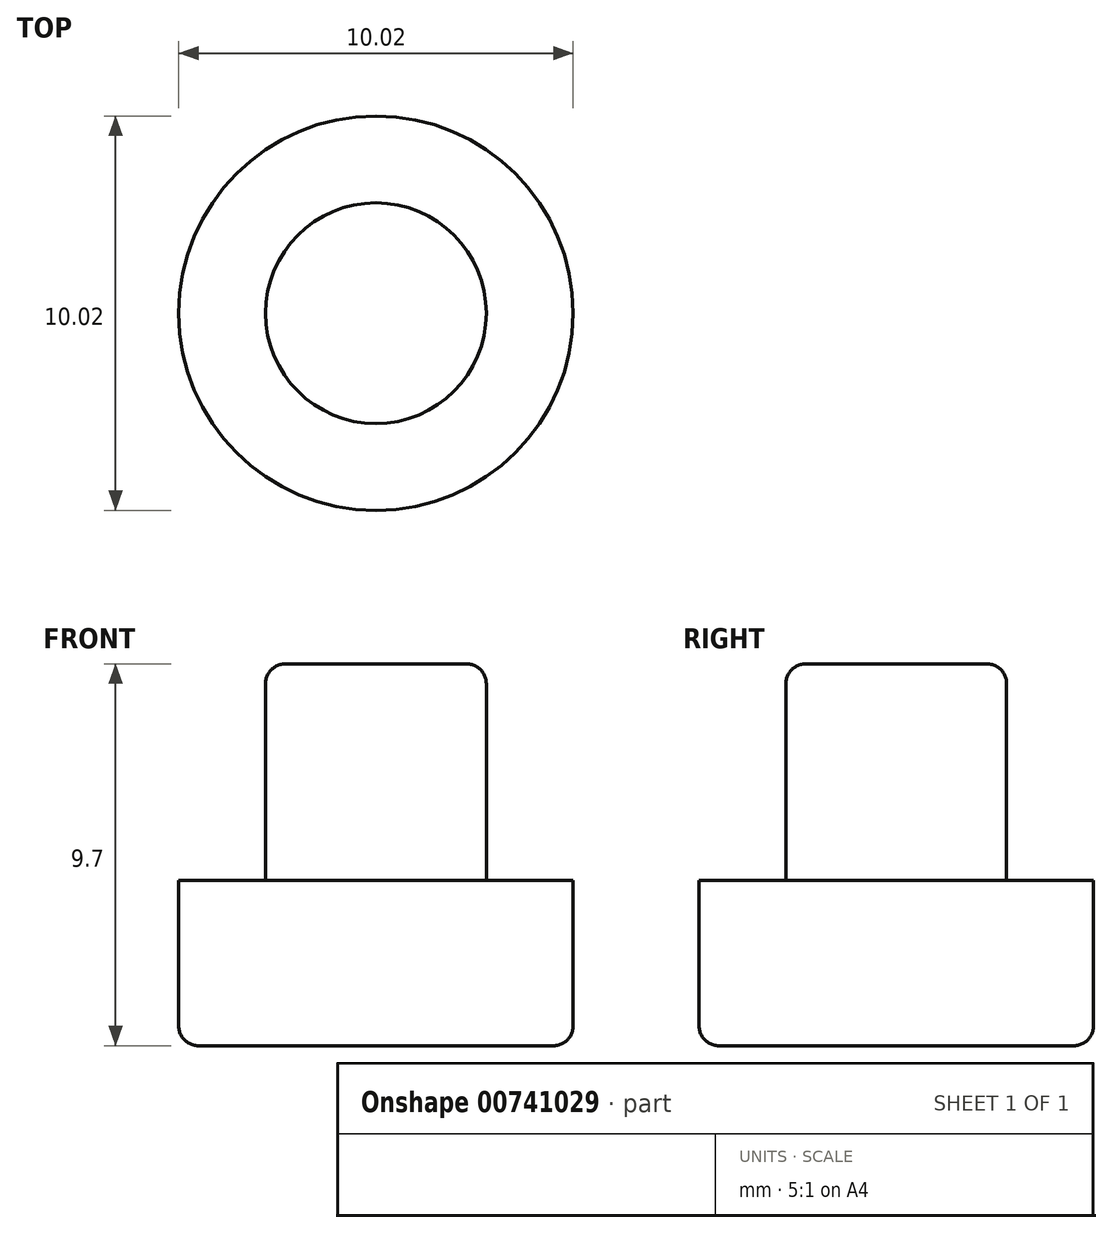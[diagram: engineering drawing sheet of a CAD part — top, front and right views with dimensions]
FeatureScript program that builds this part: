
annotation { "Feature Type Name" : "Feature", "Feature Type Description" : "" }
export const myFeature = defineFeature(function(context is Context, id is Id, definition is map)
    precondition{}
    {
        {
            var Q0;
            Q0=qCreatedBy(makeId("Top.planeOp"),FACE);
            var sketch = newSketch(context, id + "F0", { "sketchPlane" : qUnion([Q0])});
            skCircle(sketch, "E0", {"center": v(0, 0) * mm, "radius": 5.01 * mm});
            skSolve(sketch);
        }
        {
            var Q0;
            Q0 = qSketchRegion(id + "F0", true);
            extrude(context, id + "F1", {"entities" : qUnion([Q0]), "depth" : 4.2 * mm, "offsetDistance" : 25 * mm});
        }
        {
            var Q0;
            Q0=makeQuery(id+"F1.opExtrude","CAP_FACE",FACE,{"disambiguationData":[OSD([sQuery(id+"F0.wireOp",EDGE,"E0")])],"isStart":false});
            var sketch = newSketch(context, id + "F2", { "sketchPlane" : qUnion([Q0])});
            skCircle(sketch, "E1", {"center": v(0, 0) * mm, "radius": 2.8 * mm});
            skSolve(sketch);
        }
        {
            var Q0;
            Q0 = qSketchRegion(id + "F2", true);
            extrude(context, id + "F3", {"entities" : qUnion([Q0]), "operationType" : NewBodyOperationType.ADD, "depth" : 5.5 * mm, "offsetDistance" : 25 * mm});
        }
        {
            var Q0;
            Q0=makeQuery(id+"F3.opExtrude","CAP_EDGE",EDGE,{"disambiguationData":[OSD([sQuery(id+"F2.wireOp",EDGE,"E1")])],"isStart":false});
            var Q1;
            Q1=makeQuery(id+"F1.opExtrude","CAP_EDGE",EDGE,{"disambiguationData":[OSD([sQuery(id+"F0.wireOp",EDGE,"E0")])],"isStart":true});
            fillet(context, id + "F4", {"entities" : qUnion([Q0, Q1]), "radius" : .5 * mm, "tangentPropagation" : true, "allowEdgeOverflow" : false});
        }
    });
